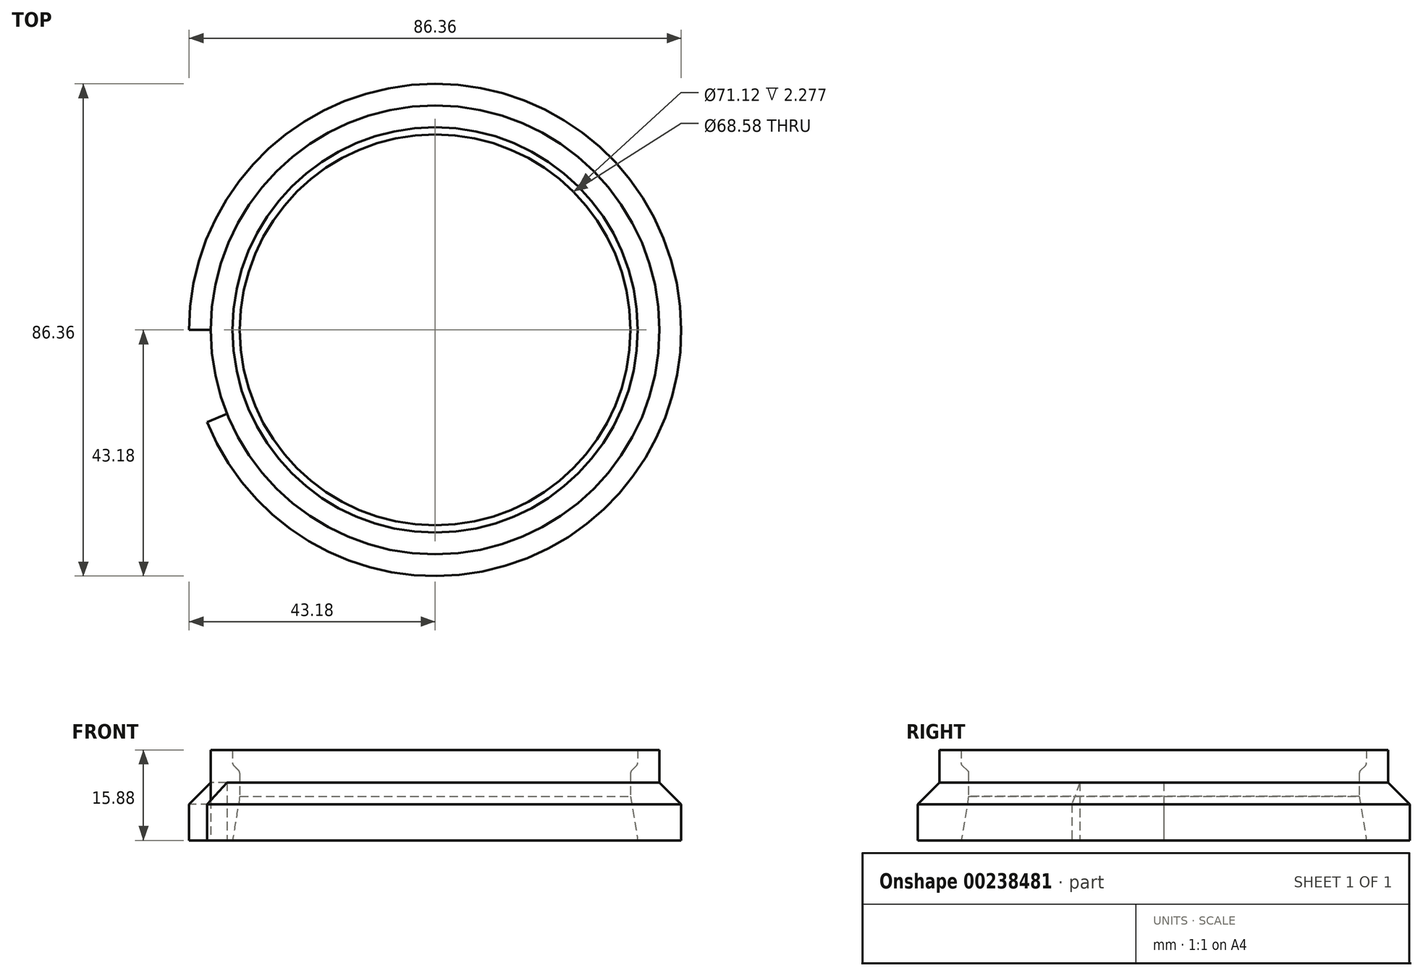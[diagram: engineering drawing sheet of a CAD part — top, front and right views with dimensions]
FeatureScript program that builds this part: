
annotation { "Feature Type Name" : "Feature", "Feature Type Description" : "" }
export const myFeature = defineFeature(function(context is Context, id is Id, definition is map)
    precondition{}
    {
        {
            var Q0;
            Q0=qCreatedBy(makeId("Front.planeOp"),FACE);
            var sketch = newSketch(context, id + "F0", { "sketchPlane" : qUnion([Q0])});
            skLineSegment(sketch, "E0", {"start": v(-43.18, 0) * mm, "end": v(-43.18, 15.88) * mm});
            skLineSegment(sketch, "E1", {"start": v(-43.18, 15.88) * mm, "end": v(-35.56, 15.88) * mm});
            skLineSegment(sketch, "E2", {"start": v(-35.56, 0) * mm, "end": v(-43.18, 0) * mm});
            skLineSegment(sketch, "E3", {"start": v(-34.48, 12.25) * mm, "end": v(-35.37, 13.15) * mm});
            skLineSegment(sketch, "E4", {"start": v(-35.56, 15.88) * mm, "end": v(-35.56, 13.6) * mm});
            skLineSegment(sketch, "E5", {"start": v(-34.3, 11.8) * mm, "end": v(-34.3, 7.75) * mm});
            skLineSegment(sketch, "E6", {"start": v(0, -4.7) * mm, "end": v(0, 44.98) * mm, "construction": true});
            skPoint(sketch, "E7.visualSharp", {"position": v(-35.56, 13.33) * mm});
            skArc(sketch, "E7.filletArc", {"start": v(-35.56, 13.6) * mm, "mid": v(-35.51, 13.36) * mm, "end": v(-35.37, 13.15) * mm});
            skPoint(sketch, "E8.visualSharp", {"position": v(-34.3, 12.07) * mm});
            skArc(sketch, "E8.filletArc", {"start": v(-34.3, 11.8) * mm, "mid": v(-34.34, 12.04) * mm, "end": v(-34.48, 12.25) * mm});
            skLineSegment(sketch, "E9", {"start": v(-34.3, 7.75) * mm, "end": v(-35.56, 0) * mm});
            skSolve(sketch);
        }
        {
            var Q0;
            Q0 = qSketchRegion(id + "F0", true);
            var Q1;
            Q1=sQuery(id+"F0.wireOp",EDGE,"E6");
            revolve(context, id + "F1", {"entities" : qUnion([Q0]), "axis" : qUnion([Q1]), "revolveType" : RevolveType.FULL});
        }
        {
            var Q0;
            Q0=makeQuery(id+"F1.opRevolve","SWEPT_FACE",FACE,{"disambiguationData":[OSD([sQuery(id+"F0.wireOp",EDGE,"E2")])]});
            var sketch = newSketch(context, id + "F2", { "sketchPlane" : qUnion([Q0])});
            skLineSegment(sketch, "E10", {"start": v(-39.37, 0) * mm, "end": v(-49.91, 0) * mm});
            skLineSegment(sketch, "E11", {"start": v(-36.5, 14.75) * mm, "end": v(-46.28, 18.7) * mm});
            skArc(sketch, "E12", {"start": v(-36.5, 14.75) * mm, "mid": v(-38.65, 7.51) * mm, "end": v(-39.37, 0) * mm});
            skArc(sketch, "E13", {"start": v(-46.28, 18.7) * mm, "mid": v(-49, 9.52) * mm, "end": v(-49.91, 0) * mm});
            skSolve(sketch);
        }
        {
            var Q0;
            Q0 = qSketchRegion(id + "F2", true);
            extrude(context, id + "F3", {"entities" : qUnion([Q0]), "operationType" : NewBodyOperationType.REMOVE, "oppositeDirection" : true, "depth" : 25.4 * mm});
        }
        {
            var Q0;
            Q0=qCreatedBy(makeId("Top.planeOp"),FACE);
            var sketch = newSketch(context, id + "F4", { "sketchPlane" : qUnion([Q0])});
            skCircle(sketch, "E14", {"center": v(0, 0) * mm, "radius": 39.37 * mm});
            skCircle(sketch, "E15", {"center": v(0, 0) * mm, "radius": 48.94 * mm});
            skSolve(sketch);
        }
        {
            var Q0;
            Q0=qCreatedBy(makeId("Right.planeOp"),FACE);
            var sketch = newSketch(context, id + "F5", { "sketchPlane" : qUnion([Q0])});
            skLineSegment(sketch, "E16", {"start": v(39.37, 10.16) * mm, "end": v(43.18, 6.35) * mm});
            skLineSegment(sketch, "E17", {"start": v(43.18, 15.88) * mm, "end": v(43.18, 6.35) * mm});
            skLineSegment(sketch, "E18", {"start": v(43.18, 15.88) * mm, "end": v(39.37, 15.88) * mm});
            skLineSegment(sketch, "E19", {"start": v(39.37, 15.88) * mm, "end": v(39.37, 10.16) * mm});
            skSolve(sketch);
        }
        {
            var Q0;
            Q0 = qSketchRegion(id + "F5", true);
            var Q1;
            Q1=sQuery(id+"F0.wireOp",EDGE,"E6");
            revolve(context, id + "F6", {"operationType" : NewBodyOperationType.REMOVE, "entities" : qUnion([Q0]), "axis" : qUnion([Q1]), "revolveType" : RevolveType.FULL, "oppositeDirection" : true});
        }
    });
